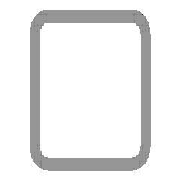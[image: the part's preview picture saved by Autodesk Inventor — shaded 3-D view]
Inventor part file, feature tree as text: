
AUTODESK INVENTOR PART (.ipt)
format: ipt  version: 2025 (Build 290162010, 162A)  size: 134,656 bytes
history: native  units: mm (DEFAULTED — no unit token found)
features: other x4, sketch x1, plane x1
ambient origin geometry x8: Origin, YZ Plane, XZ Plane, XY Plane, X Axis, Y Axis, Z Axis, Center Point
bodies: Solid1 (feature_tree), Body (feature_tree)
feature tree (6):
  parser-record x1  (decoder bookkeeping rows leaked as tree rows — omitted from the tree; the rows remain in map.json)
  other  "Driven Length"
  other  "Start Plane"
  other  "End Plane"
  sketch  "Sketch3"  dims[d3=850.0mm d4=0.0mm d7=8.0mm d9=100.0mm d11=100.0mm d12=4.0mm d13=50.0mm d14=900.0mm d15=50.0mm d16=50.0mm d17=90.0deg d18=850.0mm]
  plane  "Work Plane3"
